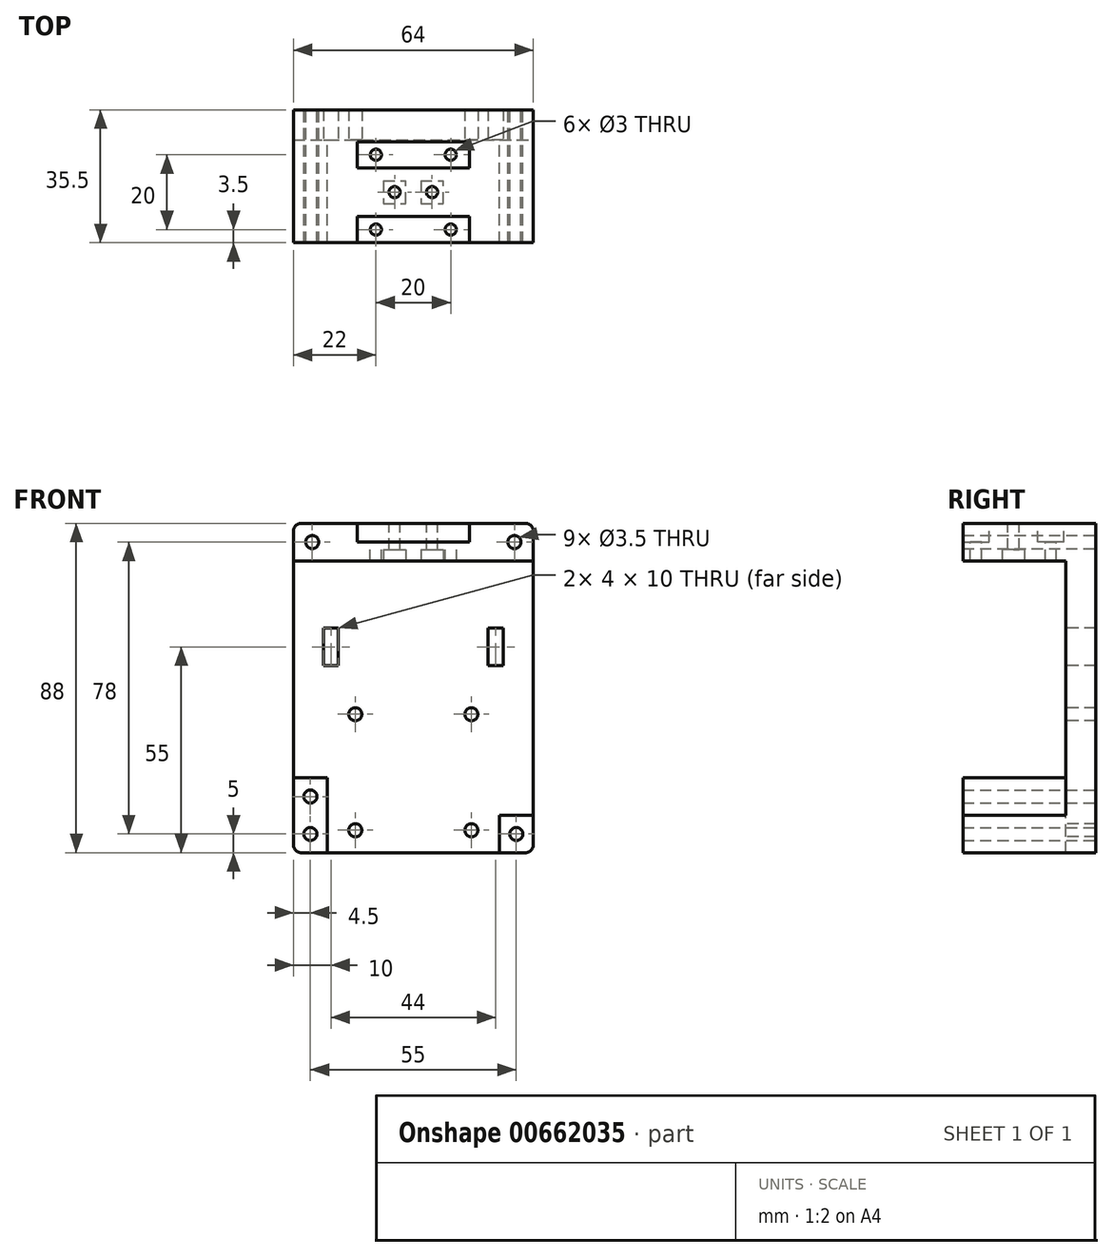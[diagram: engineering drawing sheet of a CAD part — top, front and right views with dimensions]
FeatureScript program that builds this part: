
annotation { "Feature Type Name" : "Feature", "Feature Type Description" : "" }
export const myFeature = defineFeature(function(context is Context, id is Id, definition is map)
    precondition{}
    {
        {
            var Q0;
            Q0=qCreatedBy(makeId("Front.planeOp"),FACE);
            var sketch = newSketch(context, id + "F0", { "sketchPlane" : qUnion([Q0])});
            skLineSegment(sketch, "E0.bottom", {"start": v(-32, 44) * mm, "end": v(32, 44) * mm});
            skLineSegment(sketch, "E0.top", {"start": v(-32, -44) * mm, "end": v(32, -44) * mm});
            skLineSegment(sketch, "E0.left", {"start": v(-32, 44) * mm, "end": v(-32, -44) * mm});
            skLineSegment(sketch, "E0.right", {"start": v(32, 44) * mm, "end": v(32, -44) * mm});
            skPoint(sketch, "E0.middle", {"position": v(0, 0) * mm});
            skSolve(sketch);
        }
        {
            var Q0;
            Q0 = qSketchRegion(id + "F0", true);
            extrude(context, id + "F1", {"entities" : qUnion([Q0]), "depth" : 8 * mm, "offsetDistance" : 25 * mm});
        }
        {
            var Q0;
            Q0=makeQuery(id+"F1.opExtrude","CAP_FACE",FACE,{"disambiguationData":[OSD([sQuery(id+"F0.wireOp",EDGE,"E0.bottom"),sQuery(id+"F0.wireOp",EDGE,"E0.top"),sQuery(id+"F0.wireOp",EDGE,"E0.left"),sQuery(id+"F0.wireOp",EDGE,"E0.right")])],"isStart":false});
            var sketch = newSketch(context, id + "F2", { "sketchPlane" : qUnion([Q0])});
            skLineSegment(sketch, "E1.bottom", {"start": v(-32, 44) * mm, "end": v(32, 44) * mm});
            skLineSegment(sketch, "E1.top", {"start": v(-32, 34) * mm, "end": v(32, 34) * mm});
            skLineSegment(sketch, "E1.left", {"start": v(-32, 44) * mm, "end": v(-32, 34) * mm});
            skLineSegment(sketch, "E1.right", {"start": v(32, 44) * mm, "end": v(32, 34) * mm});
            skLineSegment(sketch, "E2", {"start": v(-32, 44) * mm, "end": v(-27, 44) * mm});
            skLineSegment(sketch, "E3", {"start": v(32, 44) * mm, "end": v(27, 44) * mm});
            skPoint(sketch, "E4.centerSnap0", {"position": v(-32, 39) * mm});
            skLineSegment(sketch, "E5.bottom", {"start": v(-32, -44) * mm, "end": v(-23, -44) * mm});
            skLineSegment(sketch, "E5.top", {"start": v(-32, -24) * mm, "end": v(-23, -24) * mm});
            skLineSegment(sketch, "E5.left", {"start": v(-32, -44) * mm, "end": v(-32, -24) * mm});
            skLineSegment(sketch, "E5.right", {"start": v(-23, -44) * mm, "end": v(-23, -24) * mm});
            skLineSegment(sketch, "E6.bottom", {"start": v(32, -44) * mm, "end": v(23, -44) * mm});
            skLineSegment(sketch, "E6.left", {"start": v(32, -44) * mm, "end": v(32, -34) * mm});
            skLineSegment(sketch, "E6.right", {"start": v(23, -44) * mm, "end": v(23, -34) * mm});
            skLineSegment(sketch, "E7", {"start": v(23, -34) * mm, "end": v(23, -34) * mm});
            skCircle(sketch, "E8", {"center": v(27.5, -39) * mm, "radius": 1.75 * mm});
            skPoint(sketch, "E8.centerSnap0", {"position": v(27.5, -44) * mm});
            skPoint(sketch, "E8.centerSnap1", {"position": v(23, -39) * mm});
            skCircle(sketch, "E9", {"center": v(-27.5, -29) * mm, "radius": 1.75 * mm});
            skPoint(sketch, "E9.centerSnap0", {"position": v(-27.5, -24) * mm});
            skCircle(sketch, "E10", {"center": v(-27.5, -39) * mm, "radius": 1.75 * mm});
            skPoint(sketch, "E10.centerSnap0", {"position": v(-27.5, -44) * mm});
            skCircle(sketch, "E11", {"center": v(27, 39) * mm, "radius": 1.75 * mm});
            skCircle(sketch, "E12", {"center": v(-27, 39) * mm, "radius": 1.75 * mm});
            skLineSegment(sketch, "E13", {"start": v(23, -34) * mm, "end": v(32, -34) * mm});
            skLineSegment(sketch, "E14", {"start": v(-27, 39) * mm, "end": v(27, 39) * mm});
            skLineSegment(sketch, "E15", {"start": v(-27.5, -39) * mm, "end": v(-27.5, -44) * mm});
            skSolve(sketch);
        }
        {
            var Q0;
            {var subQ5=sQuery(id+"F2.wireOp",EDGE,"E1.bottom");Q0=makeQuery(id+"F2.imprint","IMPRINT",FACE,{"disambiguationData":[TD([[makeQuery(id+"F2.imprint","IMPRINT",EDGE,{"derivedFrom":subQ5}),-1.0]])]});}
            var Q1;
            {var subQ7=sQuery(id+"F2.wireOp",EDGE,"E1.left");Q1=makeQuery(id+"F2.imprint","IMPRINT",FACE,{"disambiguationData":[TD([[makeQuery(id+"F2.imprint","IMPRINT",EDGE,{"derivedFrom":subQ7}),1.0]])]});}
            var Q2;
            {var subQ4=sQuery(id+"F2.wireOp",EDGE,"E1.right");Q2=makeQuery(id+"F2.imprint","IMPRINT",FACE,{"disambiguationData":[TD([[makeQuery(id+"F2.imprint","IMPRINT",EDGE,{"derivedFrom":subQ4}),-1.0]])]});}
            var Q3;
            {var subQ0=sQuery(id+"F2.wireOp",EDGE,"Yd16WVRt-REVt-OFJK-DjKu-hKXUaHA9P329.left");Q3=makeQuery(id+"F2.imprint","IMPRINT",FACE,{"disambiguationData":[TD([[makeQuery(id+"F2.imprint","IMPRINT",EDGE,{"derivedFrom":subQ0}),1.0]])]});}
            var Q4;
            {var subQ5=sQuery(id+"F2.wireOp",EDGE,"Yd16WVRt-REVt-OFJK-DjKu-hKXUaHA9P329.right");Q4=makeQuery(id+"F2.imprint","IMPRINT",FACE,{"disambiguationData":[TD([[makeQuery(id+"F2.imprint","IMPRINT",EDGE,{"derivedFrom":subQ5}),1.0]])]});}
            var Q5;
            {var subQ5=sQuery(id+"F2.wireOp",EDGE,"CasWpeyr-yzLB-Kpzk-7YAV-Q1AeIs8uSEGq.right");Q5=makeQuery(id+"F2.imprint","IMPRINT",FACE,{"disambiguationData":[TD([[makeQuery(id+"F2.imprint","IMPRINT",EDGE,{"derivedFrom":subQ5}),-1.0]])]});}
            var Q6;
            {var subQ0=sQuery(id+"F2.wireOp",EDGE,"CasWpeyr-yzLB-Kpzk-7YAV-Q1AeIs8uSEGq.left");Q6=makeQuery(id+"F2.imprint","IMPRINT",FACE,{"disambiguationData":[TD([[makeQuery(id+"F2.imprint","IMPRINT",EDGE,{"derivedFrom":subQ0}),-1.0]])]});}
            var Q7;
            Q7=makeQuery(id+"F2.imprint","IMPRINT",FACE,{"disambiguationData":[TD([[makeQuery(id+"F2.imprint","IMPRINT",EDGE,{"derivedFrom":sQuery(id+"F2.wireOp",EDGE,"E5.bottom")}),1.0]])]});
            var Q8;
            Q8=makeQuery(id+"F2.imprint","IMPRINT",FACE,{"disambiguationData":[TD([[makeQuery(id+"F2.imprint","IMPRINT",EDGE,{"derivedFrom":sQuery(id+"F2.wireOp",EDGE,"E6.bottom")}),1.0]])]});
            extrude(context, id + "F3", {"entities" : qUnion([Q0, Q1, Q2, Q3, Q4, Q5, Q6, Q7, Q8]), "operationType" : NewBodyOperationType.ADD, "depth" : 27.5 * mm, "offsetDistance" : 25 * mm});
        }
        {
            var Q0;
            Q0=makeQuery(id+"F3.boolean.opBoolean","MERGE",FACE,{"derivedFrom":[makeQuery(id+"F1.opExtrude","SWEPT_FACE",FACE,{"disambiguationData":[OSD([sQuery(id+"F0.wireOp",EDGE,"E0.bottom")])]}),makeQuery(id+"F3.opExtrude","SWEPT_FACE",FACE,{"disambiguationData":[OSD([sQuery(id+"F2.wireOp",EDGE,"E1.bottom"),sQuery(id+"F2.wireOp",EDGE,"E2"),sQuery(id+"F2.wireOp",EDGE,"E3")])]})]});
            var sketch = newSketch(context, id + "F4", { "sketchPlane" : qUnion([Q0])});
            skLineSegment(sketch, "E16", {"start": v(0, -35.5) * mm, "end": v(-22, -35.5) * mm});
            skLineSegment(sketch, "E17", {"start": v(0, -35.5) * mm, "end": v(22, -35.5) * mm});
            skLineSegment(sketch, "E18", {"start": v(22, -35.5) * mm, "end": v(22, -8.5) * mm});
            skLineSegment(sketch, "E19", {"start": v(22, -8.5) * mm, "end": v(-22, -8.5) * mm});
            skLineSegment(sketch, "E20", {"start": v(-22, -8.5) * mm, "end": v(-22, -35.5) * mm});
            skLineSegment(sketch, "E21", {"start": v(-22, -22) * mm, "end": v(-22, -12) * mm});
            skLineSegment(sketch, "E22", {"start": v(-22, -22) * mm, "end": v(-22, -32) * mm});
            skLineSegment(sketch, "E23", {"start": v(-22, -12) * mm, "end": v(22, -12) * mm});
            skLineSegment(sketch, "E24", {"start": v(-22, -32) * mm, "end": v(22, -32) * mm});
            skLineSegment(sketch, "E25", {"start": v(0, -12) * mm, "end": v(-10, -12) * mm});
            skLineSegment(sketch, "E26", {"start": v(0, -12) * mm, "end": v(10, -12) * mm});
            skLineSegment(sketch, "E27", {"start": v(-10, -12) * mm, "end": v(-10, -32) * mm});
            skLineSegment(sketch, "E28", {"start": v(10, -12) * mm, "end": v(10, -32) * mm});
            skCircle(sketch, "E29", {"center": v(-10, -12) * mm, "radius": 1.5 * mm});
            skCircle(sketch, "E30", {"center": v(10, -12) * mm, "radius": 1.5 * mm});
            skCircle(sketch, "E31", {"center": v(10, -32) * mm, "radius": 1.5 * mm});
            skCircle(sketch, "E32", {"center": v(-10, -32) * mm, "radius": 1.5 * mm});
            skSolve(sketch);
        }
        {
            var Q0;
            {var subQ1=sQuery(id+"F4.wireOp",EDGE,"E23");var subQ3=sQuery(id+"F4.wireOp",EDGE,"E29");var subQ4=makeQuery(id+"F4.imprint","INTERSECT",VERTEX,{"derivedFrom":[subQ1,subQ3]});Q0=makeQuery(id+"F4.imprint","IMPRINT",FACE,{"disambiguationData":[TD([[makeQuery(id+"F4.imprint","IMPRINT",EDGE,{"disambiguationData":[TD([[subQ4,-1.0]])],"derivedFrom":subQ3}),1.0]])]});}
            var Q1;
            {var subQ1=sQuery(id+"F4.wireOp",EDGE,"E25");var subQ3=sQuery(id+"F4.wireOp",EDGE,"E29");var subQ4=makeQuery(id+"F4.imprint","INTERSECT",VERTEX,{"derivedFrom":[subQ1,subQ3]});Q1=makeQuery(id+"F4.imprint","IMPRINT",FACE,{"disambiguationData":[TD([[makeQuery(id+"F4.imprint","IMPRINT",EDGE,{"disambiguationData":[TD([[subQ4,1.0]])],"derivedFrom":subQ3}),1.0]])]});}
            var Q2;
            {var subQ1=sQuery(id+"F4.wireOp",EDGE,"E23");var subQ3=sQuery(id+"F4.wireOp",EDGE,"E29");var subQ4=makeQuery(id+"F4.imprint","INTERSECT",VERTEX,{"derivedFrom":[subQ1,subQ3]});Q2=makeQuery(id+"F4.imprint","IMPRINT",FACE,{"disambiguationData":[TD([[makeQuery(id+"F4.imprint","IMPRINT",EDGE,{"disambiguationData":[TD([[subQ4,1.0]])],"derivedFrom":subQ3}),1.0]])]});}
            var Q3;
            {var subQ0=sQuery(id+"F4.wireOp",EDGE,"E24");var subQ1=makeQuery(id+"F4.imprint","INTERSECT",VERTEX,{"derivedFrom":[subQ0,sQuery(id+"F4.wireOp",EDGE,"E27")]});Q3=makeQuery(id+"F4.imprint","IMPRINT",FACE,{"disambiguationData":[TD([[makeQuery(id+"F4.imprint","IMPRINT",EDGE,{"disambiguationData":[TD([[subQ1,1.0]])],"derivedFrom":subQ0}),-1.0]])]});}
            var Q4;
            {var subQ0=sQuery(id+"F4.wireOp",EDGE,"E27");var subQ1=sQuery(id+"F4.wireOp",EDGE,"E24");var subQ2=makeQuery(id+"F4.imprint","INTERSECT",VERTEX,{"derivedFrom":[subQ1,subQ0]});Q4=makeQuery(id+"F4.imprint","IMPRINT",FACE,{"disambiguationData":[TD([[makeQuery(id+"F4.imprint","IMPRINT",EDGE,{"disambiguationData":[TD([[subQ2,1.0]])],"derivedFrom":subQ1}),1.0]])]});}
            var Q5;
            {var subQ0=sQuery(id+"F4.wireOp",EDGE,"E27");var subQ1=sQuery(id+"F4.wireOp",EDGE,"E24");var subQ2=makeQuery(id+"F4.imprint","INTERSECT",VERTEX,{"derivedFrom":[subQ1,subQ0]});Q5=makeQuery(id+"F4.imprint","IMPRINT",FACE,{"disambiguationData":[TD([[makeQuery(id+"F4.imprint","IMPRINT",EDGE,{"disambiguationData":[TD([[subQ2,-1.0]])],"derivedFrom":subQ1}),1.0]])]});}
            var Q6;
            {var subQ0=sQuery(id+"F4.wireOp",EDGE,"E28");var subQ1=sQuery(id+"F4.wireOp",EDGE,"E24");var subQ2=makeQuery(id+"F4.imprint","INTERSECT",VERTEX,{"derivedFrom":[subQ1,subQ0]});Q6=makeQuery(id+"F4.imprint","IMPRINT",FACE,{"disambiguationData":[TD([[makeQuery(id+"F4.imprint","IMPRINT",EDGE,{"disambiguationData":[TD([[subQ2,1.0]])],"derivedFrom":subQ1}),1.0]])]});}
            var Q7;
            {var subQ0=sQuery(id+"F4.wireOp",EDGE,"E28");var subQ1=sQuery(id+"F4.wireOp",EDGE,"E24");var subQ2=makeQuery(id+"F4.imprint","INTERSECT",VERTEX,{"derivedFrom":[subQ1,subQ0]});Q7=makeQuery(id+"F4.imprint","IMPRINT",FACE,{"disambiguationData":[TD([[makeQuery(id+"F4.imprint","IMPRINT",EDGE,{"disambiguationData":[TD([[subQ2,-1.0]])],"derivedFrom":subQ1}),1.0]])]});}
            var Q8;
            {var subQ0=sQuery(id+"F4.wireOp",EDGE,"E24");var subQ1=makeQuery(id+"F4.imprint","INTERSECT",VERTEX,{"derivedFrom":[subQ0,sQuery(id+"F4.wireOp",EDGE,"E28")]});Q8=makeQuery(id+"F4.imprint","IMPRINT",FACE,{"disambiguationData":[TD([[makeQuery(id+"F4.imprint","IMPRINT",EDGE,{"disambiguationData":[TD([[subQ1,1.0]])],"derivedFrom":subQ0}),-1.0]])]});}
            var Q9;
            {var subQ1=sQuery(id+"F4.wireOp",EDGE,"E26");var subQ3=sQuery(id+"F4.wireOp",EDGE,"E30");var subQ4=makeQuery(id+"F4.imprint","INTERSECT",VERTEX,{"derivedFrom":[subQ1,subQ3]});Q9=makeQuery(id+"F4.imprint","IMPRINT",FACE,{"disambiguationData":[TD([[makeQuery(id+"F4.imprint","IMPRINT",EDGE,{"disambiguationData":[TD([[subQ4,-1.0]])],"derivedFrom":subQ3}),1.0]])]});}
            var Q10;
            {var subQ1=sQuery(id+"F4.wireOp",EDGE,"E23");var subQ3=sQuery(id+"F4.wireOp",EDGE,"E30");var subQ4=makeQuery(id+"F4.imprint","INTERSECT",VERTEX,{"derivedFrom":[subQ1,subQ3]});Q10=makeQuery(id+"F4.imprint","IMPRINT",FACE,{"disambiguationData":[TD([[makeQuery(id+"F4.imprint","IMPRINT",EDGE,{"disambiguationData":[TD([[subQ4,1.0]])],"derivedFrom":subQ3}),1.0]])]});}
            var Q11;
            {var subQ1=sQuery(id+"F4.wireOp",EDGE,"E23");var subQ3=sQuery(id+"F4.wireOp",EDGE,"E30");var subQ4=makeQuery(id+"F4.imprint","INTERSECT",VERTEX,{"derivedFrom":[subQ1,subQ3]});Q11=makeQuery(id+"F4.imprint","IMPRINT",FACE,{"disambiguationData":[TD([[makeQuery(id+"F4.imprint","IMPRINT",EDGE,{"disambiguationData":[TD([[subQ4,-1.0]])],"derivedFrom":subQ3}),1.0]])]});}
            extrude(context, id + "F5", {"entities" : qUnion([Q0, Q1, Q2, Q3, Q4, Q5, Q6, Q7, Q8, Q9, Q10, Q11]), "operationType" : NewBodyOperationType.REMOVE, "oppositeDirection" : true, "depth" : 25 * mm, "offsetDistance" : 25 * mm});
        }
        {
            var Q0;
            Q0=makeQuery(id+"F3.boolean.opBoolean","MERGE",FACE,{"derivedFrom":[makeQuery(id+"F1.opExtrude","SWEPT_FACE",FACE,{"disambiguationData":[OSD([sQuery(id+"F0.wireOp",EDGE,"E0.bottom")])]}),makeQuery(id+"F3.opExtrude","SWEPT_FACE",FACE,{"disambiguationData":[OSD([sQuery(id+"F2.wireOp",EDGE,"E1.bottom"),sQuery(id+"F2.wireOp",EDGE,"E2"),sQuery(id+"F2.wireOp",EDGE,"E3")])]})]});
            var sketch = newSketch(context, id + "F6", { "sketchPlane" : qUnion([Q0])});
            skLineSegment(sketch, "E33", {"start": v(0, -35.5) * mm, "end": v(-15, -35.5) * mm});
            skLineSegment(sketch, "E34", {"start": v(0, -35.5) * mm, "end": v(15, -35.5) * mm});
            skLineSegment(sketch, "E35", {"start": v(-15, -35.5) * mm, "end": v(-15, -28.5) * mm});
            skLineSegment(sketch, "E36", {"start": v(-15, -28.5) * mm, "end": v(15, -28.5) * mm});
            skLineSegment(sketch, "E37", {"start": v(15, -28.5) * mm, "end": v(15, -35.5) * mm});
            skLineSegment(sketch, "E38", {"start": v(-10, -12) * mm, "end": v(-15, -12) * mm});
            skLineSegment(sketch, "E39", {"start": v(-15, -12) * mm, "end": v(-15, -8.5) * mm});
            skLineSegment(sketch, "E40", {"start": v(-15, -8.5) * mm, "end": v(-15, -15.5) * mm});
            skLineSegment(sketch, "E41", {"start": v(10, -12) * mm, "end": v(15, -12) * mm});
            skLineSegment(sketch, "E42", {"start": v(15, -12) * mm, "end": v(15, -15.5) * mm});
            skLineSegment(sketch, "E43", {"start": v(15, -15.5) * mm, "end": v(15, -8.5) * mm});
            skLineSegment(sketch, "E44", {"start": v(15, -8.5) * mm, "end": v(-15, -8.5) * mm});
            skLineSegment(sketch, "E45", {"start": v(-15, -15.5) * mm, "end": v(15, -15.5) * mm});
            skSolve(sketch);
        }
        {
            var Q0;
            Q0 = qSketchRegion(id + "F6", true);
            extrude(context, id + "F7", {"entities" : qUnion([Q0]), "operationType" : NewBodyOperationType.REMOVE, "oppositeDirection" : true, "depth" : 5 * mm, "offsetDistance" : 25 * mm});
        }
        {
            var Q0;
            Q0=makeQuery(id+"F3.boolean.opBoolean","MERGE",FACE,{"derivedFrom":[makeQuery(id+"F1.opExtrude","SWEPT_FACE",FACE,{"disambiguationData":[OSD([sQuery(id+"F0.wireOp",EDGE,"E0.bottom")])]}),makeQuery(id+"F3.opExtrude","SWEPT_FACE",FACE,{"disambiguationData":[OSD([sQuery(id+"F2.wireOp",EDGE,"E1.bottom"),sQuery(id+"F2.wireOp",EDGE,"E2"),sQuery(id+"F2.wireOp",EDGE,"E3")])]})]});
            var sketch = newSketch(context, id + "F8", { "sketchPlane" : qUnion([Q0])});
            skLineSegment(sketch, "E46", {"start": v(15, -15.5) * mm, "end": v(15, -28.5) * mm});
            skLineSegment(sketch, "E47", {"start": v(5, -22) * mm, "end": v(0, -22) * mm});
            skCircle(sketch, "E48", {"center": v(-5, -22) * mm, "radius": 1.5 * mm});
            skCircle(sketch, "E49", {"center": v(5, -22) * mm, "radius": 1.5 * mm});
            skLineSegment(sketch, "E50", {"start": v(0, -15.5) * mm, "end": v(0, -22) * mm});
            skLineSegment(sketch, "E51", {"start": v(0, -22) * mm, "end": v(-5, -22) * mm});
            skSolve(sketch);
        }
        {
            var Q0;
            Q0 = qSketchRegion(id + "F8", true);
            extrude(context, id + "F9", {"entities" : qUnion([Q0]), "operationType" : NewBodyOperationType.REMOVE, "oppositeDirection" : true, "depth" : 25 * mm, "offsetDistance" : 25 * mm});
        }
        {
            var Q0;
            Q0=makeQuery(id+"F3.opExtrude","SWEPT_FACE",FACE,{"disambiguationData":[OSD([sQuery(id+"F2.wireOp",EDGE,"E1.top")])]});
            var sketch = newSketch(context, id + "F10", { "sketchPlane" : qUnion([Q0])});
            skLineSegment(sketch, "E52", {"start": v(5, 22) * mm, "end": v(8, 22) * mm});
            skLineSegment(sketch, "E53", {"start": v(8, 22) * mm, "end": v(-5, 22) * mm});
            skLineSegment(sketch, "E54", {"start": v(-5, 22) * mm, "end": v(-8, 22) * mm});
            skLineSegment(sketch, "E55", {"start": v(-8, 22) * mm, "end": v(-8, 25) * mm});
            skLineSegment(sketch, "E56", {"start": v(5, 22) * mm, "end": v(2, 22) * mm});
            skLineSegment(sketch, "E57", {"start": v(-5, 22) * mm, "end": v(-2, 22) * mm});
            skLineSegment(sketch, "E58", {"start": v(2, 22) * mm, "end": v(2, 25) * mm});
            skLineSegment(sketch, "E59", {"start": v(2, 25) * mm, "end": v(8, 25) * mm});
            skLineSegment(sketch, "E60", {"start": v(-8, 25) * mm, "end": v(-2, 25) * mm});
            skLineSegment(sketch, "E61", {"start": v(8, 25) * mm, "end": v(8, 22) * mm});
            skLineSegment(sketch, "E62", {"start": v(-8, 22) * mm, "end": v(-8, 19) * mm});
            skLineSegment(sketch, "E63", {"start": v(-8, 19) * mm, "end": v(-2, 19) * mm});
            skLineSegment(sketch, "E64", {"start": v(-2, 19) * mm, "end": v(-2, 22) * mm});
            skLineSegment(sketch, "E65", {"start": v(2, 22) * mm, "end": v(2, 19) * mm});
            skLineSegment(sketch, "E66", {"start": v(2, 19) * mm, "end": v(8, 19) * mm});
            skLineSegment(sketch, "E67", {"start": v(8, 19) * mm, "end": v(8, 22) * mm});
            skLineSegment(sketch, "E68", {"start": v(-2, 25) * mm, "end": v(-2, 22) * mm});
            skSolve(sketch);
        }
        {
            var Q0;
            Q0 = qSketchRegion(id + "F10", true);
            extrude(context, id + "F11", {"entities" : qUnion([Q0]), "operationType" : NewBodyOperationType.REMOVE, "oppositeDirection" : true, "depth" : 3 * mm, "offsetDistance" : 25 * mm});
        }
        {
            var Q0;
            Q0=makeQuery(id+"F3.boolean.opBoolean","SPLIT",FACE,{"disambiguationData":[TD([makeQuery(id+"F3.opExtrude","SWEPT_FACE",FACE,{"disambiguationData":[OSD([sQuery(id+"F2.wireOp",EDGE,"E4")])]})])],"derivedFrom":makeQuery(id+"F1.opExtrude","CAP_FACE",FACE,{"disambiguationData":[OSD([sQuery(id+"F0.wireOp",EDGE,"E0.bottom"),sQuery(id+"F0.wireOp",EDGE,"E0.top"),sQuery(id+"F0.wireOp",EDGE,"E0.left"),sQuery(id+"F0.wireOp",EDGE,"E0.right")])],"isStart":false})});
            var Q1;
            Q1=makeQuery(id+"F3.boolean.opBoolean","SPLIT",FACE,{"disambiguationData":[TD([makeQuery(id+"F3.opExtrude","SWEPT_FACE",FACE,{"disambiguationData":[OSD([sQuery(id+"F2.wireOp",EDGE,"ZvZAWqEd-CA94-Rpaa-SU6f-6qopx4zODHrz")])]})])],"derivedFrom":makeQuery(id+"F1.opExtrude","CAP_FACE",FACE,{"disambiguationData":[OSD([sQuery(id+"F0.wireOp",EDGE,"E0.bottom"),sQuery(id+"F0.wireOp",EDGE,"E0.top"),sQuery(id+"F0.wireOp",EDGE,"E0.left"),sQuery(id+"F0.wireOp",EDGE,"E0.right")])],"isStart":false})});
            var Q2;
            Q2=makeQuery(id+"F3.boolean.opBoolean","SPLIT",FACE,{"disambiguationData":[TD([makeQuery(id+"F3.opExtrude","SWEPT_FACE",FACE,{"disambiguationData":[OSD([sQuery(id+"F2.wireOp",EDGE,"Sl0mf3Jw-zp51-E5IY-kPNq-jfKYS2Xht1Hv")])]})])],"derivedFrom":makeQuery(id+"F1.opExtrude","CAP_FACE",FACE,{"disambiguationData":[OSD([sQuery(id+"F0.wireOp",EDGE,"E0.bottom"),sQuery(id+"F0.wireOp",EDGE,"E0.top"),sQuery(id+"F0.wireOp",EDGE,"E0.left"),sQuery(id+"F0.wireOp",EDGE,"E0.right")])],"isStart":false})});
            var Q3;
            Q3=makeQuery(id+"F3.boolean.opBoolean","SPLIT",FACE,{"disambiguationData":[TD([makeQuery(id+"F3.opExtrude","SWEPT_FACE",FACE,{"disambiguationData":[OSD([sQuery(id+"F2.wireOp",EDGE,"ueuH1zhY-iWYn-hRMC-Si5H-fBq8uUvHrsYg")])]})])],"derivedFrom":makeQuery(id+"F1.opExtrude","CAP_FACE",FACE,{"disambiguationData":[OSD([sQuery(id+"F0.wireOp",EDGE,"E0.bottom"),sQuery(id+"F0.wireOp",EDGE,"E0.top"),sQuery(id+"F0.wireOp",EDGE,"E0.left"),sQuery(id+"F0.wireOp",EDGE,"E0.right")])],"isStart":false})});
            var Q4;
            Q4=makeQuery(id+"F3.boolean.opBoolean","SPLIT",FACE,{"disambiguationData":[TD([makeQuery(id+"F3.opExtrude","SWEPT_FACE",FACE,{"disambiguationData":[OSD([sQuery(id+"F2.wireOp",EDGE,"FCoazugY-MPN5-JA2A-m2Li-t61wZpry6vJ0")])]})])],"derivedFrom":makeQuery(id+"F1.opExtrude","CAP_FACE",FACE,{"disambiguationData":[OSD([sQuery(id+"F0.wireOp",EDGE,"E0.bottom"),sQuery(id+"F0.wireOp",EDGE,"E0.top"),sQuery(id+"F0.wireOp",EDGE,"E0.left"),sQuery(id+"F0.wireOp",EDGE,"E0.right")])],"isStart":false})});
            var Q5;
            Q5=makeQuery(id+"F3.boolean.opBoolean","SPLIT",FACE,{"disambiguationData":[TD([makeQuery(id+"F3.opExtrude","SWEPT_FACE",FACE,{"disambiguationData":[OSD([sQuery(id+"F2.wireOp",EDGE,"NHk6pnkp-Mi0x-RU7y-kxS4-8469h8htnUJA")])]})])],"derivedFrom":makeQuery(id+"F1.opExtrude","CAP_FACE",FACE,{"disambiguationData":[OSD([sQuery(id+"F0.wireOp",EDGE,"E0.bottom"),sQuery(id+"F0.wireOp",EDGE,"E0.top"),sQuery(id+"F0.wireOp",EDGE,"E0.left"),sQuery(id+"F0.wireOp",EDGE,"E0.right")])],"isStart":false})});
            var Q6;
            Q6=makeQuery(id+"F3.boolean.opBoolean","SPLIT",FACE,{"disambiguationData":[TD([makeQuery(id+"F3.opExtrude","SWEPT_FACE",FACE,{"disambiguationData":[OSD([sQuery(id+"F2.wireOp",EDGE,"E8")])]})])],"derivedFrom":makeQuery(id+"F1.opExtrude","CAP_FACE",FACE,{"disambiguationData":[OSD([sQuery(id+"F0.wireOp",EDGE,"E0.bottom"),sQuery(id+"F0.wireOp",EDGE,"E0.top"),sQuery(id+"F0.wireOp",EDGE,"E0.left"),sQuery(id+"F0.wireOp",EDGE,"E0.right")])],"isStart":false})});
            var Q7;
            Q7=makeQuery(id+"F3.boolean.opBoolean","SPLIT",FACE,{"disambiguationData":[TD([makeQuery(id+"F3.opExtrude","SWEPT_FACE",FACE,{"disambiguationData":[OSD([sQuery(id+"F2.wireOp",EDGE,"K1OWNs7A-DZ5T-bWwp-Ejm7-NK7mQgMPgbh3")])]})])],"derivedFrom":makeQuery(id+"F1.opExtrude","CAP_FACE",FACE,{"disambiguationData":[OSD([sQuery(id+"F0.wireOp",EDGE,"E0.bottom"),sQuery(id+"F0.wireOp",EDGE,"E0.top"),sQuery(id+"F0.wireOp",EDGE,"E0.left"),sQuery(id+"F0.wireOp",EDGE,"E0.right")])],"isStart":false})});
            var Q8;
            Q8=makeQuery(id+"F3.boolean.opBoolean","SPLIT",FACE,{"disambiguationData":[TD([makeQuery(id+"F3.opExtrude","SWEPT_FACE",FACE,{"disambiguationData":[OSD([sQuery(id+"F2.wireOp",EDGE,"E9")])]})])],"derivedFrom":makeQuery(id+"F1.opExtrude","CAP_FACE",FACE,{"disambiguationData":[OSD([sQuery(id+"F0.wireOp",EDGE,"E0.bottom"),sQuery(id+"F0.wireOp",EDGE,"E0.top"),sQuery(id+"F0.wireOp",EDGE,"E0.left"),sQuery(id+"F0.wireOp",EDGE,"E0.right")])],"isStart":false})});
            var Q9;
            Q9=makeQuery(id+"F3.boolean.opBoolean","SPLIT",FACE,{"disambiguationData":[TD([makeQuery(id+"F3.opExtrude","SWEPT_FACE",FACE,{"disambiguationData":[OSD([sQuery(id+"F2.wireOp",EDGE,"E10")])]})])],"derivedFrom":makeQuery(id+"F1.opExtrude","CAP_FACE",FACE,{"disambiguationData":[OSD([sQuery(id+"F0.wireOp",EDGE,"E0.bottom"),sQuery(id+"F0.wireOp",EDGE,"E0.top"),sQuery(id+"F0.wireOp",EDGE,"E0.left"),sQuery(id+"F0.wireOp",EDGE,"E0.right")])],"isStart":false})});
            var Q10;
            Q10=makeQuery(id+"F3.boolean.opBoolean","SPLIT",FACE,{"disambiguationData":[TD([makeQuery(id+"F3.opExtrude","SWEPT_FACE",FACE,{"disambiguationData":[OSD([sQuery(id+"F2.wireOp",EDGE,"E11")])]})])],"derivedFrom":makeQuery(id+"F1.opExtrude","CAP_FACE",FACE,{"disambiguationData":[OSD([sQuery(id+"F0.wireOp",EDGE,"E0.bottom"),sQuery(id+"F0.wireOp",EDGE,"E0.top"),sQuery(id+"F0.wireOp",EDGE,"E0.left"),sQuery(id+"F0.wireOp",EDGE,"E0.right")])],"isStart":false})});
            var Q11;
            Q11=makeQuery(id+"F3.boolean.opBoolean","SPLIT",FACE,{"disambiguationData":[TD([makeQuery(id+"F3.opExtrude","SWEPT_FACE",FACE,{"disambiguationData":[OSD([sQuery(id+"F2.wireOp",EDGE,"E12")])]})])],"derivedFrom":makeQuery(id+"F1.opExtrude","CAP_FACE",FACE,{"disambiguationData":[OSD([sQuery(id+"F0.wireOp",EDGE,"E0.bottom"),sQuery(id+"F0.wireOp",EDGE,"E0.top"),sQuery(id+"F0.wireOp",EDGE,"E0.left"),sQuery(id+"F0.wireOp",EDGE,"E0.right")])],"isStart":false})});
            extrude(context, id + "F12", {"entities" : qUnion([Q0, Q1, Q2, Q3, Q4, Q5, Q6, Q7, Q8, Q9, Q10, Q11]), "operationType" : NewBodyOperationType.REMOVE, "oppositeDirection" : true, "depth" : 25 * mm, "offsetDistance" : 25 * mm});
        }
        {
            var Q0;
            {var subQ0=sQuery(id+"F0.wireOp",EDGE,"E0.top");var subQ1=sQuery(id+"F0.wireOp",EDGE,"E0.right");var subQ2=sQuery(id+"F0.wireOp",EDGE,"E0.left");Q0=makeQuery(id+"F3.boolean.opBoolean","SPLIT",FACE,{"disambiguationData":[TD([makeQuery(id+"F1.opExtrude","SWEPT_FACE",FACE,{"disambiguationData":[OSD([subQ0])]})])],"derivedFrom":makeQuery(id+"F1.opExtrude","CAP_FACE",FACE,{"disambiguationData":[OSD([sQuery(id+"F0.wireOp",EDGE,"E0.bottom"),subQ0,subQ2,subQ1])],"isStart":false})});}
            var sketch = newSketch(context, id + "F13", { "sketchPlane" : qUnion([Q0])});
            skLineSegment(sketch, "E69", {"start": v(0, 34) * mm, "end": v(0, -1) * mm});
            skLineSegment(sketch, "E70", {"start": v(32, -1) * mm, "end": v(-32, -1) * mm});
            skLineSegment(sketch, "E71", {"start": v(0, -1) * mm, "end": v(-21.5, -1) * mm});
            skLineSegment(sketch, "E72", {"start": v(-21.5, -1) * mm, "end": v(21.5, -1) * mm});
            skLineSegment(sketch, "E73", {"start": v(21.5, -1) * mm, "end": v(21.5, -44) * mm});
            skLineSegment(sketch, "E74", {"start": v(21.5, -44) * mm, "end": v(-21.5, -44) * mm});
            skLineSegment(sketch, "E75", {"start": v(-21.5, -44) * mm, "end": v(-21.5, -1) * mm});
            skLineSegment(sketch, "E76.bottom", {"start": v(-15.5, -7) * mm, "end": v(15.5, -7) * mm});
            skLineSegment(sketch, "E76.top", {"start": v(-15.5, -38) * mm, "end": v(15.5, -38) * mm});
            skLineSegment(sketch, "E76.left", {"start": v(-15.5, -7) * mm, "end": v(-15.5, -38) * mm});
            skLineSegment(sketch, "E76.right", {"start": v(15.5, -7) * mm, "end": v(15.5, -38) * mm});
            skPoint(sketch, "E76.middle", {"position": v(0, -22.5) * mm});
            skPoint(sketch, "E76.middle.positionSnap0", {"position": v(0, -44) * mm});
            skPoint(sketch, "E76.middle.positionSnap1", {"position": v(-21.5, -22.5) * mm});
            skPoint(sketch, "E76.centerSnap0", {"position": v(0, -44) * mm});
            skPoint(sketch, "E76.centerSnap1", {"position": v(-21.5, -22.5) * mm});
            skCircle(sketch, "E77", {"center": v(-15.5, -7) * mm, "radius": 1.75 * mm});
            skCircle(sketch, "E78", {"center": v(15.5, -7) * mm, "radius": 1.75 * mm});
            skCircle(sketch, "E79", {"center": v(-15.5, -38) * mm, "radius": 1.75 * mm});
            skCircle(sketch, "E80", {"center": v(15.5, -38) * mm, "radius": 1.75 * mm});
            skSolve(sketch);
        }
        {
            var Q0;
            {var subQ0=sQuery(id+"F13.wireOp",EDGE,"E76.left");var subQ1=sQuery(id+"F13.wireOp",EDGE,"E76.bottom");var subQ2=makeQuery(id+"F13.imprint","INTERSECT",VERTEX,{"derivedFrom":[subQ1,subQ0]});Q0=makeQuery(id+"F13.imprint","IMPRINT",FACE,{"disambiguationData":[TD([[makeQuery(id+"F13.imprint","IMPRINT",EDGE,{"disambiguationData":[TD([[subQ2,-1.0]])],"derivedFrom":subQ1}),1.0]])]});}
            var Q1;
            {var subQ0=sQuery(id+"F13.wireOp",EDGE,"E76.left");var subQ1=sQuery(id+"F13.wireOp",EDGE,"E76.bottom");var subQ2=makeQuery(id+"F13.imprint","INTERSECT",VERTEX,{"derivedFrom":[subQ1,subQ0]});Q1=makeQuery(id+"F13.imprint","IMPRINT",FACE,{"disambiguationData":[TD([[makeQuery(id+"F13.imprint","IMPRINT",EDGE,{"disambiguationData":[TD([[subQ2,-1.0]])],"derivedFrom":subQ1}),-1.0]])]});}
            var Q2;
            {var subQ0=sQuery(id+"F13.wireOp",EDGE,"E76.right");var subQ1=sQuery(id+"F13.wireOp",EDGE,"E76.bottom");var subQ2=makeQuery(id+"F13.imprint","INTERSECT",VERTEX,{"derivedFrom":[subQ1,subQ0]});Q2=makeQuery(id+"F13.imprint","IMPRINT",FACE,{"disambiguationData":[TD([[makeQuery(id+"F13.imprint","IMPRINT",EDGE,{"disambiguationData":[TD([[subQ2,1.0]])],"derivedFrom":subQ1}),-1.0]])]});}
            var Q3;
            {var subQ0=sQuery(id+"F13.wireOp",EDGE,"E76.right");var subQ1=sQuery(id+"F13.wireOp",EDGE,"E76.bottom");var subQ2=makeQuery(id+"F13.imprint","INTERSECT",VERTEX,{"derivedFrom":[subQ1,subQ0]});Q3=makeQuery(id+"F13.imprint","IMPRINT",FACE,{"disambiguationData":[TD([[makeQuery(id+"F13.imprint","IMPRINT",EDGE,{"disambiguationData":[TD([[subQ2,1.0]])],"derivedFrom":subQ1}),1.0]])]});}
            var Q4;
            {var subQ0=sQuery(id+"F13.wireOp",EDGE,"E76.right");var subQ1=sQuery(id+"F13.wireOp",EDGE,"E76.top");var subQ2=makeQuery(id+"F13.imprint","INTERSECT",VERTEX,{"derivedFrom":[subQ1,subQ0]});Q4=makeQuery(id+"F13.imprint","IMPRINT",FACE,{"disambiguationData":[TD([[makeQuery(id+"F13.imprint","IMPRINT",EDGE,{"disambiguationData":[TD([[subQ2,1.0]])],"derivedFrom":subQ1}),1.0]])]});}
            var Q5;
            {var subQ0=sQuery(id+"F13.wireOp",EDGE,"E76.right");var subQ1=sQuery(id+"F13.wireOp",EDGE,"E76.top");var subQ2=makeQuery(id+"F13.imprint","INTERSECT",VERTEX,{"derivedFrom":[subQ1,subQ0]});Q5=makeQuery(id+"F13.imprint","IMPRINT",FACE,{"disambiguationData":[TD([[makeQuery(id+"F13.imprint","IMPRINT",EDGE,{"disambiguationData":[TD([[subQ2,1.0]])],"derivedFrom":subQ1}),-1.0]])]});}
            var Q6;
            {var subQ0=sQuery(id+"F13.wireOp",EDGE,"E76.left");var subQ1=sQuery(id+"F13.wireOp",EDGE,"E76.top");var subQ2=makeQuery(id+"F13.imprint","INTERSECT",VERTEX,{"derivedFrom":[subQ1,subQ0]});Q6=makeQuery(id+"F13.imprint","IMPRINT",FACE,{"disambiguationData":[TD([[makeQuery(id+"F13.imprint","IMPRINT",EDGE,{"disambiguationData":[TD([[subQ2,-1.0]])],"derivedFrom":subQ1}),1.0]])]});}
            var Q7;
            {var subQ0=sQuery(id+"F13.wireOp",EDGE,"E76.left");var subQ1=sQuery(id+"F13.wireOp",EDGE,"E76.top");var subQ2=makeQuery(id+"F13.imprint","INTERSECT",VERTEX,{"derivedFrom":[subQ1,subQ0]});Q7=makeQuery(id+"F13.imprint","IMPRINT",FACE,{"disambiguationData":[TD([[makeQuery(id+"F13.imprint","IMPRINT",EDGE,{"disambiguationData":[TD([[subQ2,-1.0]])],"derivedFrom":subQ1}),-1.0]])]});}
            extrude(context, id + "F14", {"entities" : qUnion([Q0, Q1, Q2, Q3, Q4, Q5, Q6, Q7]), "operationType" : NewBodyOperationType.REMOVE, "oppositeDirection" : true, "depth" : 25 * mm, "offsetDistance" : 25 * mm});
        }
        {
            var Q0;
            {var subQ0=sQuery(id+"F0.wireOp",EDGE,"E0.top");var subQ1=sQuery(id+"F0.wireOp",EDGE,"E0.right");var subQ2=sQuery(id+"F0.wireOp",EDGE,"E0.left");Q0=makeQuery(id+"F3.boolean.opBoolean","SPLIT",FACE,{"disambiguationData":[TD([makeQuery(id+"F1.opExtrude","SWEPT_FACE",FACE,{"disambiguationData":[OSD([subQ0])]})])],"derivedFrom":makeQuery(id+"F1.opExtrude","CAP_FACE",FACE,{"disambiguationData":[OSD([sQuery(id+"F0.wireOp",EDGE,"E0.bottom"),subQ0,subQ2,subQ1])],"isStart":false})});}
            var sketch = newSketch(context, id + "F15", { "sketchPlane" : qUnion([Q0])});
            skLineSegment(sketch, "E81", {"start": v(-24, 34) * mm, "end": v(-24, 16) * mm});
            skLineSegment(sketch, "E82.bottom", {"start": v(-24, 16) * mm, "end": v(-20, 16) * mm});
            skLineSegment(sketch, "E82.top", {"start": v(-24, 6) * mm, "end": v(-20, 6) * mm});
            skLineSegment(sketch, "E82.left", {"start": v(-24, 16) * mm, "end": v(-24, 6) * mm});
            skLineSegment(sketch, "E82.right", {"start": v(-20, 16) * mm, "end": v(-20, 6) * mm});
            skLineSegment(sketch, "E83", {"start": v(24, 34) * mm, "end": v(24, 16) * mm});
            skLineSegment(sketch, "E84.bottom", {"start": v(24, 16) * mm, "end": v(20, 16) * mm});
            skLineSegment(sketch, "E84.top", {"start": v(24, 6) * mm, "end": v(20, 6) * mm});
            skLineSegment(sketch, "E84.left", {"start": v(24, 16) * mm, "end": v(24, 6) * mm});
            skLineSegment(sketch, "E84.right", {"start": v(20, 16) * mm, "end": v(20, 6) * mm});
            skLineSegment(sketch, "E85", {"start": v(-24, 27.13) * mm, "end": v(-32, 27.13) * mm});
            skLineSegment(sketch, "E86", {"start": v(24, 25) * mm, "end": v(32, 25) * mm});
            skSolve(sketch);
        }
        {
            var Q0;
            Q0 = qSketchRegion(id + "F15", true);
            extrude(context, id + "F16", {"entities" : qUnion([Q0]), "operationType" : NewBodyOperationType.REMOVE, "oppositeDirection" : true, "depth" : 25 * mm, "offsetDistance" : 25 * mm});
        }
        {
            var Q0;
            Q0=makeQuery(id+"F3.boolean.opBoolean","MERGE",EDGE,{"derivedFrom":[makeQuery(id+"F1.opExtrude","SWEPT_EDGE",EDGE,{"disambiguationData":[OSD([sQuery(id+"F0.wireOp",EDGE,"E0.top"),sQuery(id+"F0.wireOp",EDGE,"E0.right")])]}),makeQuery(id+"F3.opExtrude","SWEPT_EDGE",EDGE,{"disambiguationData":[OSD([sQuery(id+"F2.wireOp",EDGE,"E6.bottom"),sQuery(id+"F2.wireOp",EDGE,"E6.left")])]})]});
            var Q1;
            Q1=makeQuery(id+"F3.boolean.opBoolean","MERGE",EDGE,{"derivedFrom":[makeQuery(id+"F1.opExtrude","SWEPT_EDGE",EDGE,{"disambiguationData":[OSD([sQuery(id+"F0.wireOp",EDGE,"E0.bottom"),sQuery(id+"F0.wireOp",EDGE,"E0.right")])]}),makeQuery(id+"F3.opExtrude","SWEPT_EDGE",EDGE,{"disambiguationData":[OSD([sQuery(id+"F2.wireOp",EDGE,"E1.right"),sQuery(id+"F2.wireOp",EDGE,"E3")])]})]});
            var Q2;
            Q2=makeQuery(id+"F3.boolean.opBoolean","MERGE",EDGE,{"derivedFrom":[makeQuery(id+"F1.opExtrude","SWEPT_EDGE",EDGE,{"disambiguationData":[OSD([sQuery(id+"F0.wireOp",EDGE,"E0.top"),sQuery(id+"F0.wireOp",EDGE,"E0.left")])]}),makeQuery(id+"F3.opExtrude","SWEPT_EDGE",EDGE,{"disambiguationData":[OSD([sQuery(id+"F2.wireOp",EDGE,"E5.bottom"),sQuery(id+"F2.wireOp",EDGE,"E5.left")])]})]});
            var Q3;
            Q3=makeQuery(id+"F3.boolean.opBoolean","MERGE",EDGE,{"derivedFrom":[makeQuery(id+"F1.opExtrude","SWEPT_EDGE",EDGE,{"disambiguationData":[OSD([sQuery(id+"F0.wireOp",EDGE,"E0.bottom"),sQuery(id+"F0.wireOp",EDGE,"E0.left")])]}),makeQuery(id+"F3.opExtrude","SWEPT_EDGE",EDGE,{"disambiguationData":[OSD([sQuery(id+"F2.wireOp",EDGE,"E1.left"),sQuery(id+"F2.wireOp",EDGE,"E2")])]})]});
            fillet(context, id + "F17", {"entities" : qUnion([Q0, Q1, Q2, Q3]), "radius" : 2 * mm, "tangentPropagation" : true, "allowEdgeOverflow" : false});
        }
    });
